# Revit family: CENTUM Gelenkhalter längs
name_source: partatom
category: HLS-Bauteile
revit_build: Autodesk Revit 2017 (Build: 20190507_1515(x64)
units: mm (PartAtom-declared; Revit-internal decimal feet)

## family parameters
Arbeitsebenenbasiert = Ja
Beim Laden mit Abzugskörper schneiden = Nein
Bemaßung runder Anschluss = Durchmesser verwenden
Gemeinsam genutzt = Ja
Immer vertikal = Nein
Raumberechnungspunkt = Nein
Teiletyp = Normal

## types (1)
- CENTUM Gelenkhalter XL 100 längs
    Artikelnummer = 1641004010
    Ausrichtung Platte = längs
    Breite Platte = 160 mm  [stored 0.524934 ft]
    EAN = 4250928437006
    Fabrikat = MEFA
    Firma = MEFA Befestigungs- und Montagesysteme GmbH
    Gewicht = 4.89 kg
    Gewicht pro Bauteil = 4.89 kg
    Kurztext1 = Gelenkhalter CENTUM XL 100
    Kurztext2 = Platte längs max. Winkel 90 °
    Langloch Platte = 14 x 40 mm
    Länge Platte = 260 mm  [stored 0.853018 ft]
    Material = Stahl
    Mengeneinheit = St
    Oberflaeche = feuerstückverzinkt
    Profil = CENTUM
    Profiltyp = XL 100
    Sicherheitsfaktor = 1.54
    Stärke Platte = 10 mm  [stored 0.0328084 ft]
    Vorgabe-Ansicht = 1219 mm
    Winkel = 90 °
    max. zul. Last = 20.00 kN
    vpe = 1 St

note: [stored X ft] marks values corroborated as IEEE doubles in the binary element streams (Revit-internal decimal feet)
